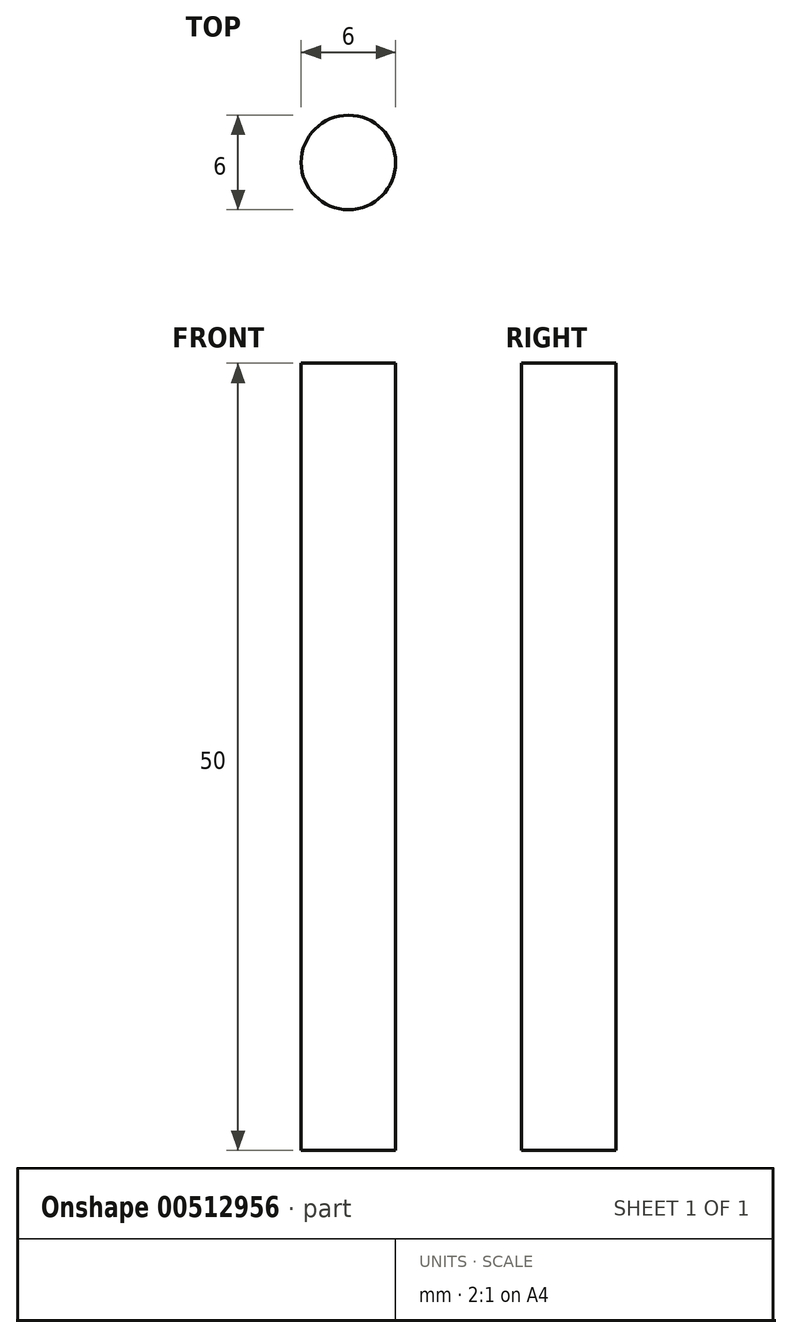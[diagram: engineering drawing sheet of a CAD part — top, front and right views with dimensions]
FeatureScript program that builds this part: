
annotation { "Feature Type Name" : "Feature", "Feature Type Description" : "" }
export const myFeature = defineFeature(function(context is Context, id is Id, definition is map)
    precondition{}
    {
        {
            var Q0;
            Q0=qCreatedBy(makeId("Top.planeOp"),FACE);
            var sketch = newSketch(context, id + "F0", { "sketchPlane" : qUnion([Q0])});
            skCircle(sketch, "E0", {"center": v(0, 0) * mm, "radius": 3 * mm});
            skSolve(sketch);
        }
        {
            var Q0;
            Q0 = qSketchRegion(id + "F0", true);
            extrude(context, id + "F1", {"entities" : qUnion([Q0]), "depth" : 50 * mm});
        }
    });
